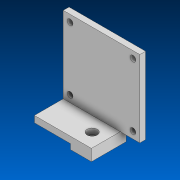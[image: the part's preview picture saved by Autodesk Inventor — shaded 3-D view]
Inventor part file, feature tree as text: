
AUTODESK INVENTOR PART (.ipt)
format: ipt  version: 2022.2 (Build 262287000, 287)  size: 124,928 bytes
history: native  units: in
note: dims shown in document units (in); Inventor stores cm internally (conversion verified against a paired STEP export)
features: sketch x3, extrude x2, hole x2
ambient origin geometry x8: Origin, YZ Plane, XZ Plane, XY Plane, X Axis, Y Axis, Z Axis, Center Point
bodies: Solid1 (feature_tree)
feature tree (7):
  sketch  "Sketch1"  dims[d1=2.65in d2=2.65in]
  extrude  "Extrusion1"  Depth=2.65in
  hole  "Hole1"  [1 undecoded]
  extrude  "Extrusion2"  Depth=0.675in
  hole  "Hole2"  [1 undecoded]
  sketch  "Sketch2"  dims[d3=2.175in d4=0.2in d5=0.0in]
  sketch  "Sketch3"  dims[d6=0.2in d7=0.75in d8=0.375in d9=0.25in d10=0.5635in d11=1.0in d12=0.8108in d14=0.675in d16=0.4in d17=0.18in d18=1.25in d19=1.2in d20=0.0in d21=0.25in d22=0.5in d23=0.18in d24=0.75in d25=0.35in d26=0.2in d27=0.5635in d28=1.0in d29=0.8108in]
note: 2 required parameter values undecoded (feature->parameter linkage not recoverable at this tier; creation-order binding heuristic only, values carry confidence <= 0.55)
